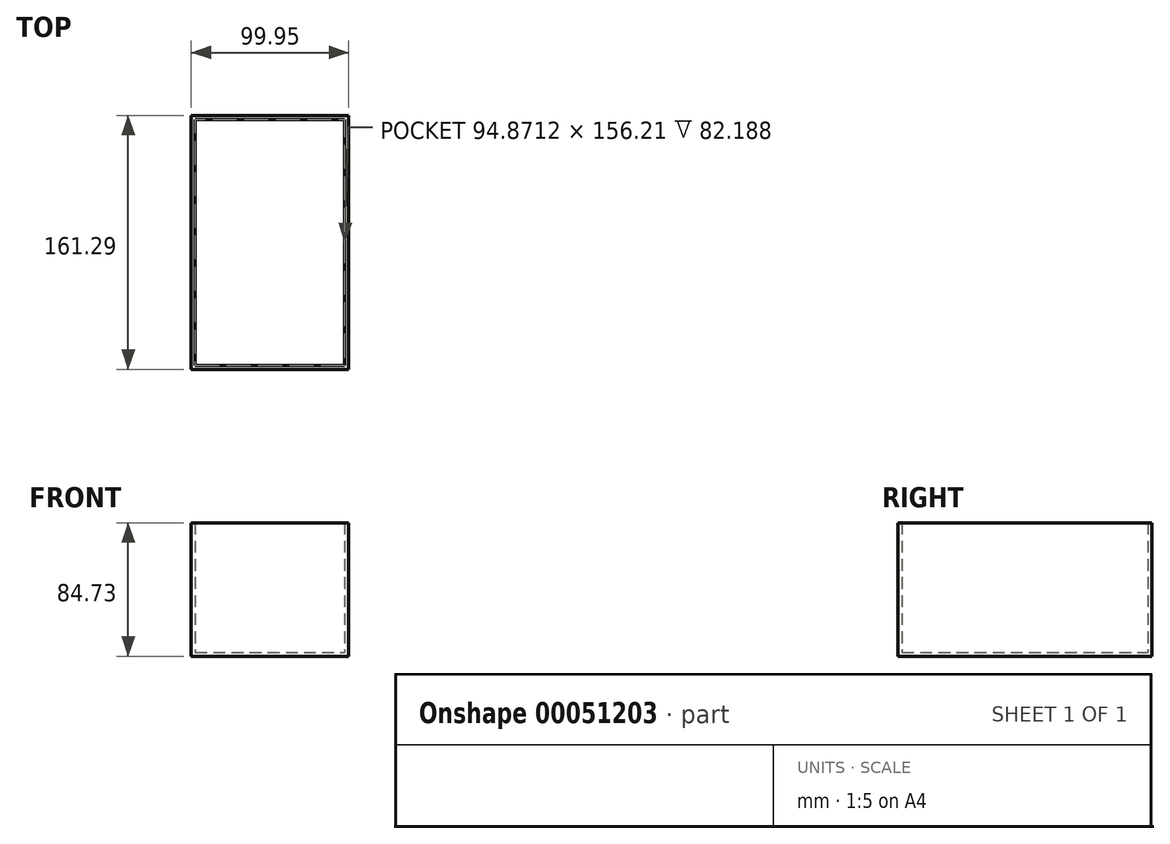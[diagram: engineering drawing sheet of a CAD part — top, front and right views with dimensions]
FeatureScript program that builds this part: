
annotation { "Feature Type Name" : "Feature", "Feature Type Description" : "" }
export const myFeature = defineFeature(function(context is Context, id is Id, definition is map)
    precondition{}
    {
        {
            var Q0;
            Q0=qCreatedBy(makeId("Front.planeOp"),FACE);
            var sketch = newSketch(context, id + "F0", { "sketchPlane" : qUnion([Q0])});
            skLineSegment(sketch, "E0.bottom", {"start": v(-62.2, 56.66) * mm, "end": v(37.74, 56.66) * mm});
            skLineSegment(sketch, "E0.top", {"start": v(-62.2, -28.07) * mm, "end": v(37.74, -28.07) * mm});
            skLineSegment(sketch, "E0.left", {"start": v(-62.2, 56.66) * mm, "end": v(-62.2, -28.07) * mm});
            skLineSegment(sketch, "E0.right", {"start": v(37.74, 56.66) * mm, "end": v(37.74, -28.07) * mm});
            skSolve(sketch);
        }
        {
            var Q0;
            Q0 = qSketchRegion(id + "F0", true);
            extrude(context, id + "F1", {"entities" : qUnion([Q0]), "depth" : 161.29 * mm});
        }
        {
            var Q0;
            Q0=makeQuery(id+"F1.opExtrude","SWEPT_FACE",FACE,{"disambiguationData":[OSD([sQuery(id+"F0.wireOp",EDGE,"E0.bottom")])]});
            shell(context, id + "F2", {"entities" : qUnion([Q0]), "thickness" : 2.54 * mm});
        }
    });
